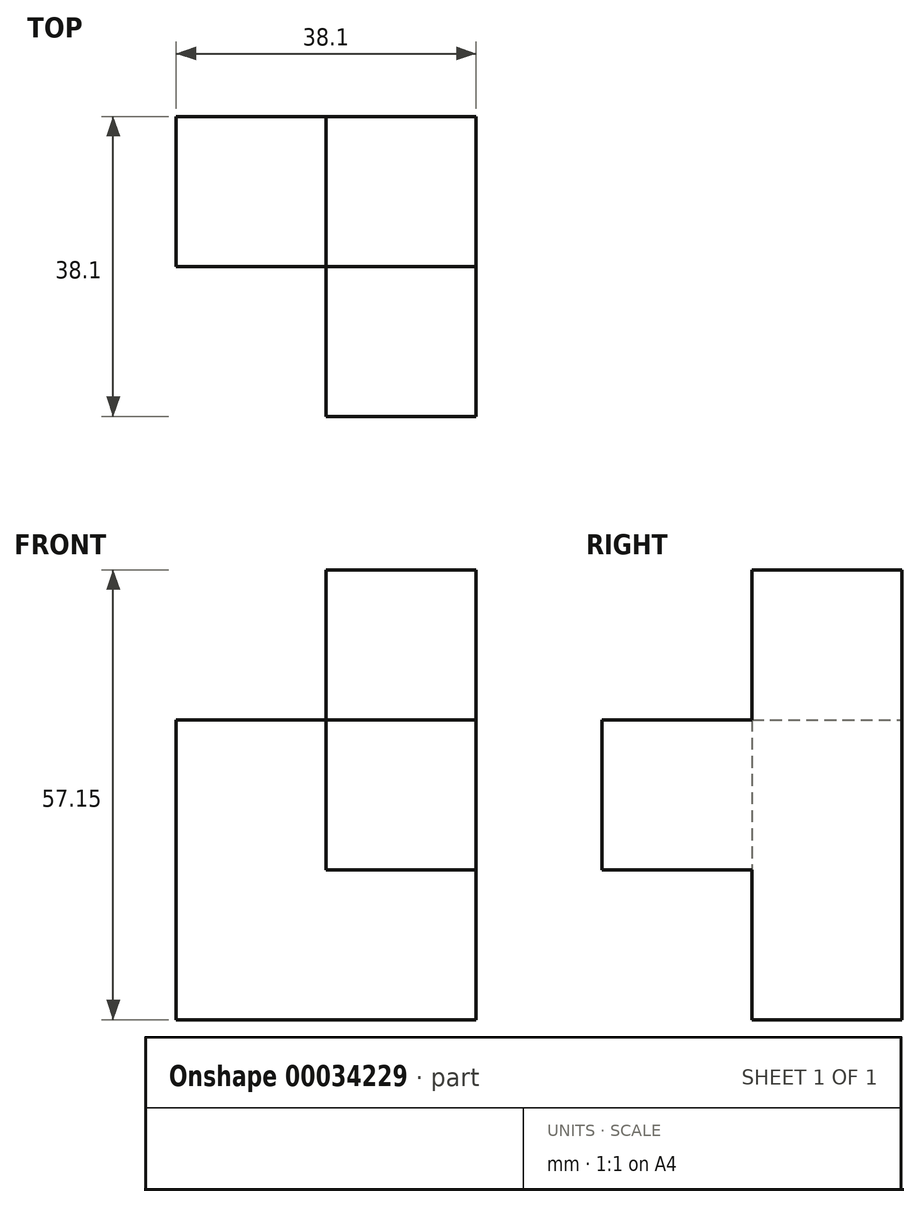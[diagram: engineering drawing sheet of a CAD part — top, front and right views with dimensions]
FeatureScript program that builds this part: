
annotation { "Feature Type Name" : "Feature", "Feature Type Description" : "" }
export const myFeature = defineFeature(function(context is Context, id is Id, definition is map)
    precondition{}
    {
        {
            var Q0;
            Q0=qCreatedBy(makeId("Front.planeOp"),FACE);
            var sketch = newSketch(context, id + "F0", { "sketchPlane" : qUnion([Q0])});
            skLineSegment(sketch, "E0.bottom", {"start": v(-38.1, 38.1) * mm, "end": v(0, 38.1) * mm});
            skLineSegment(sketch, "E0.top", {"start": v(-38.1, 0) * mm, "end": v(0, 0) * mm});
            skLineSegment(sketch, "E0.left", {"start": v(-38.1, 38.1) * mm, "end": v(-38.1, 0) * mm});
            skLineSegment(sketch, "E0.right", {"start": v(0, 38.1) * mm, "end": v(0, 0) * mm});
            skLineSegment(sketch, "E1.bottom", {"start": v(-38.1, 38.1) * mm, "end": v(-19.05, 38.1) * mm});
            skLineSegment(sketch, "E1.top", {"start": v(-38.1, 57.15) * mm, "end": v(-19.05, 57.15) * mm});
            skLineSegment(sketch, "E1.left", {"start": v(-38.1, 38.1) * mm, "end": v(-38.1, 57.15) * mm});
            skLineSegment(sketch, "E1.right", {"start": v(-19.05, 38.1) * mm, "end": v(-19.05, 57.15) * mm});
            skSolve(sketch);
        }
        {
            var Q0;
            Q0 = qSketchRegion(id + "F0", true);
            extrude(context, id + "F1", {"entities" : qUnion([Q0]), "oppositeDirection" : true, "depth" : 19.05 * mm});
        }
        {
            var Q0;
            Q0=qCreatedBy(makeId("Front.planeOp"),FACE);
            var sketch = newSketch(context, id + "F2", { "sketchPlane" : qUnion([Q0])});
            skLineSegment(sketch, "E2.bottom", {"start": v(-19.05, 38.1) * mm, "end": v(-38.1, 38.1) * mm});
            skLineSegment(sketch, "E2.top", {"start": v(-19.05, 19.05) * mm, "end": v(-38.1, 19.05) * mm});
            skLineSegment(sketch, "E2.left", {"start": v(-19.05, 38.1) * mm, "end": v(-19.05, 19.05) * mm});
            skLineSegment(sketch, "E2.right", {"start": v(-38.1, 38.1) * mm, "end": v(-38.1, 19.05) * mm});
            skSolve(sketch);
        }
        {
            var Q0;
            Q0 = qSketchRegion(id + "F2", true);
            extrude(context, id + "F3", {"entities" : qUnion([Q0]), "operationType" : NewBodyOperationType.ADD, "oppositeDirection" : true, "depth" : 38.1 * mm});
        }
        {
            var Q0;
            Q0=makeQuery(id+"F1.opExtrude","SWEPT_BODY",BODY,{"disambiguationData":[OSD([sQuery(id+"F0.wireOp",EDGE,"E0.bottom"),sQuery(id+"F0.wireOp",EDGE,"E0.top"),sQuery(id+"F0.wireOp",EDGE,"E0.left"),sQuery(id+"F0.wireOp",EDGE,"E0.right"),sQuery(id+"F0.wireOp",EDGE,"E1.top"),sQuery(id+"F0.wireOp",EDGE,"E1.left"),sQuery(id+"F0.wireOp",EDGE,"E1.right")])]});
            var Q1;
            Q1=makeQuery(id+"F1.opExtrude","CAP_EDGE",EDGE,{"disambiguationData":[OSD([sQuery(id+"F0.wireOp",EDGE,"E0.left"),sQuery(id+"F0.wireOp",EDGE,"E1.left")])],"isStart":true});
            var Q2;
            Q2=makeQuery(id+"F1.opExtrude","CAP_EDGE",EDGE,{"disambiguationData":[OSD([sQuery(id+"F0.wireOp",EDGE,"E0.left"),sQuery(id+"F0.wireOp",EDGE,"E1.left")])],"isStart":true});
            transform(context, id + "F4", {"entities" : qUnion([Q0]), "transformType" : TransformType.ROTATION, "transformAxis" : qUnion([Q2]), "angle" : 180 * degree, "makeCopy" : false});
        }
    });
